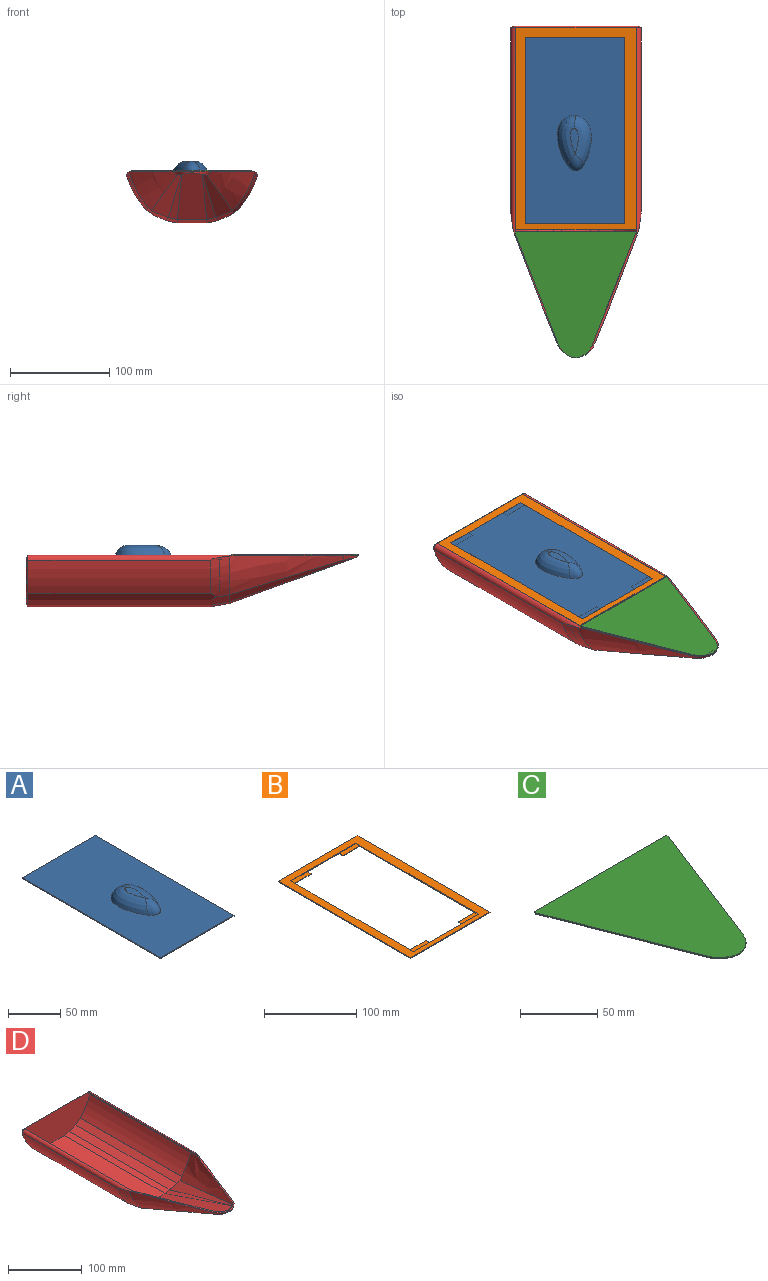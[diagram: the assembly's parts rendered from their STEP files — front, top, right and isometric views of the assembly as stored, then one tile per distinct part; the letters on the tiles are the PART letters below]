
ASSEMBLY  parts=4 mates=3
PART A: 10 faces, bbox 99.6x187.7x11.2 mm
  f0: plane 99.57x1mm, normal (0,-1,0), area 99.6mm2, adj f1,f3,f4,f5
  f1: plane 187.68x1mm, normal (1,0,0), area 187.7mm2, adj f0,f2,f4,f5
  f2: plane 99.57x1mm, normal (0,1,0), area 99.6mm2, adj f1,f3,f4,f5
  f3: plane 187.68x1mm, normal (-1,0,0), area 187.7mm2, adj f0,f2,f4,f5
  f4: plane 187.7x99.59mm, normal (0,0,1), area 17219.9mm2, adj f0,f1,f2,f3,f7,f8,f9
  f5: plane 187.68x99.57mm, normal (0,0,-1), area 18687mm2, adj f0,f1,f2,f3
  f6: plane 25.18x8.13mm, normal (0,0,1), area 142.3mm2, adj f8,f9
  f7: bspline ~17.72x17.36mm, area 167.8mm2, adj f4,f8,f9
  f8: bspline ~51.33x20.86mm, area 843.1mm2, adj f4,f6,f7,f9
  f9: bspline ~53.14x52.57mm, area 796.2mm2, adj f4,f6,f7,f8
PART B: 22 faces, bbox 121.4x203.3x1 mm
  f0: plane 99.65x1mm, normal (0,-1,0), area 74.2mm2, adj f1,f3,f4,f9,f13,f15,f19,f21
  f1: plane 187.75x1mm, normal (-1,0,0), area 182mm2, adj f0,f2,f3,f4,f16,f17,f19,f20
  f2: plane 99.65x1mm, normal (0,1,0), area 74.2mm2, adj f1,f3,f4,f9,f10,f12,f16,f18
  f3: plane 203.28x121.38mm, normal (0,0,1), area 5964.9mm2, adj f0,f1,f2,f5,f6,f7,f8,f9
  f4: plane 203.28x121.38mm, normal (0,0,-1), area 6545.5mm2, adj f0,f1,f2,f5,f6,f7,f8,f9
  f5: plane 121.38x1mm, normal (0,1,0), area 121.4mm2, adj f3,f4,f6,f8
  f6: plane 203.28x1mm, normal (-1,0,0), area 203.3mm2, adj f3,f4,f5,f7
  f7: plane 121.38x1mm, normal (0,-1,0), area 121.4mm2, adj f3,f4,f6,f8
  f8: plane 203.28x1mm, normal (1,0,0), area 203.3mm2, adj f3,f4,f5,f7
  f9: plane 187.75x1mm, normal (1,0,0), area 182mm2, adj f0,f2,f3,f4,f10,f11,f13,f14
  f10: plane 25.4x5.49mm, normal (0,0,1), area 139.3mm2, adj f2,f9,f11,f12
  f11: plane 25.4x0.5mm, normal (0,1,0), area 12.7mm2, adj f4,f9,f10,f12
  f12: plane 5.49x0.5mm, normal (1,0,0), area 2.7mm2, adj f2,f4,f10,f11
  f13: plane 25.4x5.93mm, normal (0,0,1), area 150.7mm2, adj f0,f9,f14,f15
  f14: plane 25.4x0.5mm, normal (0,-1,0), area 12.7mm2, adj f4,f9,f13,f15
  f15: plane 5.93x0.5mm, normal (1,0,0), area 3mm2, adj f0,f4,f13,f14
  f16: plane 25.4x5.49mm, normal (0,0,1), area 139.5mm2, adj f1,f2,f17,f18
  f17: plane 25.4x0.5mm, normal (0,1,0), area 12.7mm2, adj f1,f4,f16,f18
  f18: plane 5.49x0.5mm, normal (-1,0,0), area 2.7mm2, adj f2,f4,f16,f17
  f19: plane 25.4x5.95mm, normal (0,0,1), area 151.1mm2, adj f0,f1,f20,f21
  f20: plane 25.4x0.5mm, normal (0,-1,0), area 12.7mm2, adj f1,f4,f19,f21
  f21: plane 5.95x0.5mm, normal (-1,0,0), area 3mm2, adj f0,f4,f19,f20
PART C: 22 faces, bbox 121.4x127.1x1 mm
  f0: plane 3.17x2.58mm, normal (0.78,-0.63,0), area 4.1mm2, adj f1,f19,f20,f21
  f1: plane 3.93x1.98mm, normal (0.89,-0.45,0), area 4.4mm2, adj f0,f2,f20,f21
  f2: plane 112.42x43.9mm, normal (0.93,-0.36,0), area 120.7mm2, adj f1,f3,f20,f21
  f3: plane 1.79x1mm, normal (1,0,0), area 1.8mm2, adj f2,f4,f20,f21
  f4: plane 121.38x1mm, normal (0,1,0), area 121.4mm2, adj f3,f5,f20,f21
  f5: plane 1.79x1mm, normal (-1,0,0), area 1.8mm2, adj f4,f6,f20,f21
  f6: plane 112.43x43.91mm, normal (-0.93,-0.36,0), area 120.7mm2, adj f5,f7,f20,f21
  f7: plane 3.72x1.85mm, normal (-0.9,-0.45,0), area 4.2mm2, adj f6,f8,f20,f21
  f8: plane 3.05x2.39mm, normal (-0.79,-0.62,0), area 3.9mm2, adj f7,f9,f20,f21
  f9: plane 2.28x2.03mm, normal (-0.67,-0.75,0), area 3.1mm2, adj f8,f10,f20,f21
  f10: plane 3.1x1.93mm, normal (-0.53,-0.85,0), area 3.7mm2, adj f9,f11,f20,f21
  f11: plane 3.24x1.33mm, normal (-0.38,-0.93,0), area 3.5mm2, adj f10,f12,f20,f21
  f12: plane 1x0mm, normal (-0.31,-0.95,0), area 0mm2, adj f11,f13,f20,f21
  f13: plane 4.52x1mm, normal (-0.19,-0.98,0), area 4.6mm2, adj f12,f14,f20,f21
  f14: plane 3.18x1mm, normal (0.25,-0.97,0), area 3.3mm2, adj f13,f15,f20,f21
  f15: plane 1x0mm, normal (0.31,-0.95,0), area 0mm2, adj f14,f16,f20,f21
  f16: plane 3.38x1.37mm, normal (0.38,-0.93,0), area 3.6mm2, adj f15,f17,f20,f21
  f17: plane 2.88x1.76mm, normal (0.52,-0.85,0), area 3.4mm2, adj f16,f18,f20,f21
  f18: plane 2.19x1.88mm, normal (0.65,-0.76,0), area 2.9mm2, adj f17,f19,f20,f21
  f19: plane 1x0mm, normal (0.7,-0.71,0), area 0mm2, adj f0,f18,f20,f21
  f20: plane 127.13x121.38mm, normal (0,0,1), area 9226.7mm2, adj f0,f1,f2,f3,f4,f5,f6,f7
  f21: plane 127.13x121.38mm, normal (0,0,-1), area 9226.7mm2, adj f0,f1,f2,f3,f4,f5,f6,f7
PART D: 82 faces, bbox 138.5x340.2x68.2 mm
  f0: plane 127.52x49.15mm, normal (0,-1,0), area 5014.4mm2, adj f30,f31,f32,f33,f34,f35,f51,f52
  f1: plane 131.46x47.85mm, normal (0.18,0.34,0.92), area 690.9mm2, adj f6,f41,f44,f52,f55
  f2: plane 131.66x47.88mm, normal (-0.18,0.34,0.92), area 693mm2, adj f5,f6,f45,f54,f56
  f3: plane 4.3x3.32mm, normal (0.69,0.68,-0.25), area 0.6mm2, adj f4,f5,f46,f53,f62
  f4: plane 12.11x4.92mm, normal (0.14,0.93,-0.34), area 0.5mm2, adj f3,f5,f53,f54
  f5: plane 131.37x46.12mm, normal (-0.35,0.34,0.87), area 1502.5mm2, adj f2,f3,f4,f46,f47,f54
  f6: plane 137.09x49.94mm, normal (0,0.34,0.94), area 3595.6mm2, adj f1,f2,f48,f49,f50,f55,f56
  f7: plane 127.52x48.13mm, normal (0,1,0), area 4861.3mm2, adj f70,f71,f72,f73,f74,f75,f76,f77
  f8: plane 132.55x126.4mm, normal (0,0,1), area 603.8mm2, adj f9,f10,f20,f21,f27,f28,f29,f36
  f9: cylinder r=5.08mm len=210.92mm, axis (0,1,0), area 1581.9mm2, adj f8,f12,f20,f30,f69,f75
  f10: cylinder r=5.08mm len=210.92mm, axis (0,-1,0), area 1581.9mm2, adj f8,f11,f21,f31,f63,f79
  f11: cylinder r=90.14mm len=183.49mm, axis (0,-1,0), area 7050.9mm2, adj f10,f16,f63,f81
  f12: cylinder r=90.14mm len=183.49mm, axis (0,-1,0), area 7050.9mm2, adj f9,f19,f69,f73
  f13: plane 183.49x30.16mm, normal (0,0,-1), area 5534.2mm2, adj f17,f18,f66,f74
  f14: plane 183.49x12.53mm, normal (0.38,0,-0.93), area 2480.9mm2, adj f16,f17,f64,f78
  f15: plane 183.49x12.53mm, normal (-0.38,0,-0.93), area 2480.9mm2, adj f18,f19,f68,f70
  f16: plane 190.94x10.1mm, normal (0.58,0,-0.82), area 2211.8mm2, adj f11,f14,f63,f64,f80
  f17: plane 183.49x9.79mm, normal (0.19,0,-0.98), area 1829.7mm2, adj f13,f14,f65,f76
  f18: plane 183.49x9.79mm, normal (-0.19,0,-0.98), area 1829.7mm2, adj f13,f15,f67,f72
  f19: plane 190.94x10.1mm, normal (-0.58,0,-0.82), area 2211.8mm2, adj f12,f15,f68,f69,f71
  f20: cone r=39.34mm half-angle=20deg, axis (0,1,0), area 2911.3mm2, adj f8,f9,f22,f28,f69
  f21: cone r=39.34mm half-angle=20deg, axis (0,1,0), area 2911.3mm2, adj f8,f10,f23,f27,f63
  f22: plane 125.53x45.78mm, normal (-0.35,-0.34,-0.87), area 1417.5mm2, adj f20,f24,f28,f68
  f23: plane 125.53x45.78mm, normal (0.35,-0.34,-0.87), area 1417.5mm2, adj f21,f25,f27,f64
  f24: plane 123.63x45.01mm, normal (-0.18,-0.34,-0.92), area 650.4mm2, adj f22,f26,f28,f67
  f25: plane 123.63x45.01mm, normal (0.18,-0.34,-0.92), area 650.4mm2, adj f23,f26,f27,f65
  f26: plane 129.12x47.14mm, normal (0,-0.34,-0.94), area 3381.9mm2, adj f24,f25,f27,f28,f29,f66
  f27: bspline ~30.3x29.89mm, area 83.6mm2, adj f8,f21,f23,f25,f26,f29
  f28: bspline ~30.3x29.89mm, area 83.6mm2, adj f8,f20,f22,f24,f26,f29
  f29: bspline ~4.91x2.67mm, area 3.8mm2, adj f8,f26,f27,f28
  f30: plane 205.11x2.03mm, normal (1,0,0), area 408.7mm2, adj f0,f9,f32,f36
  f31: plane 205.1x2.03mm, normal (-1,0,0), area 408.7mm2, adj f0,f10,f33,f37
  f32: cylinder r=3.08mm len=203.6mm, axis (0,1,0), area 907mm2, adj f0,f30,f35,f36
  f33: cylinder r=3.08mm len=203.6mm, axis (0,-1,0), area 907mm2, adj f0,f31,f34,f37
  f34: cylinder r=88.14mm len=193.3mm, axis (0,-1,0), area 7153.1mm2, adj f0,f33,f37,f59
  f35: cylinder r=88.14mm len=193.3mm, axis (0,-1,0), area 7153.1mm2, adj f0,f32,f36,f57
  f36: cone r=37.46mm half-angle=20deg, axis (0,1,0), area 3397.3mm2, adj f8,f30,f32,f35,f39,f42,f58
  f37: cone r=37.46mm half-angle=20deg, axis (0,1,0), area 3397.3mm2, adj f8,f31,f33,f34,f38,f46,f61
  f38: offset ~34.38x33.97mm, area 41.1mm2, adj f8,f37,f40,f45,f47,f48
  f39: offset ~34.38x33.97mm, area 41.1mm2, adj f8,f36,f40,f41,f43,f49
  f40: bspline ~2.49x1.35mm, area 0.3mm2, adj f8,f38,f39,f50
  f41: extruded ~1.01x0.7mm, area 0.5mm2, adj f1,f39,f43,f49
  f42: extruded ~121.25x37.81mm, area 128.8mm2, adj f36,f43,f44,f58
  f43: extruded ~7.45x3.96mm, area 8.3mm2, adj f39,f41,f42,f44
  f44: plane 131.07x46.02mm, normal (0.35,0.34,0.87), area 1496mm2, adj f1,f42,f43,f51,f52,f58
  f45: extruded ~1.01x0.7mm, area 0.5mm2, adj f2,f38,f47,f48
  f46: extruded ~121.25x37.81mm, area 128.7mm2, adj f3,f5,f37,f47,f60,f62
  f47: extruded ~7.45x3.96mm, area 8.3mm2, adj f5,f38,f45,f46
  f48: extruded ~9.64x5.75mm, area 11.4mm2, adj f6,f38,f45,f50
  f49: extruded ~9.64x5.75mm, area 11.4mm2, adj f6,f39,f41,f50
  f50: extruded ~1.23x0.96mm, area 1.2mm2, adj f6,f40,f48,f49
  f51: plane 196.57x9.28mm, normal (0.58,0,0.82), area 2214.8mm2, adj f0,f44,f52,f57,f58
  f52: plane 193.26x12.13mm, normal (0.38,0,0.93), area 2531.1mm2, adj f0,f1,f44,f51,f55
  f53: plane 193.14x12.13mm, normal (-0.38,0,0.93), area 2527.3mm2, adj f0,f3,f4,f54,f62
  f54: plane 192.97x9.41mm, normal (-0.19,0,0.98), area 1849.5mm2, adj f0,f2,f4,f5,f53,f56
  f55: plane 193.17x9.41mm, normal (0.19,0,0.98), area 1851.4mm2, adj f0,f1,f6,f52,f56
  f56: plane 193.07x29.77mm, normal (0,0,1), area 5748.4mm2, adj f0,f2,f6,f54,f55
  f57: plane 193.3x0.98mm, normal (-0.98,0,0.19), area 193.3mm2, adj f0,f35,f51,f58
  f58: extruded ~5.17x4.5mm, area 6.4mm2, adj f36,f42,f44,f51,f57
  f59: plane 193.3x0.98mm, normal (0.98,0,-0.19), area 193.3mm2, adj f0,f34,f61,f62
  f60: plane 0.98x0.22mm, normal (-0.66,-0.74,0.13), area 0.1mm2, adj f46,f61,f62
  f61: extruded ~5.17x4.5mm, area 5.3mm2, adj f37,f59,f60,f62
  f62: plane 196.74x9.43mm, normal (-0.58,0,0.82), area 2214.2mm2, adj f0,f3,f46,f53,f59,f60,f61
  f63: cone r=90.14mm half-angle=10deg, axis (0,1,0), area 887.4mm2, adj f10,f11,f16,f21,f64
  f64: plane 19.71x17.96mm, normal (0.37,-0.17,-0.91), area 351.4mm2, adj f14,f16,f23,f63,f65
  f65: plane 19.71x10.12mm, normal (0.19,-0.17,-0.97), area 192.8mm2, adj f17,f25,f64,f66
  f66: plane 30.16x19.71mm, normal (0,-0.17,-0.98), area 596.8mm2, adj f13,f26,f65,f67
  f67: plane 19.71x10.12mm, normal (-0.19,-0.17,-0.97), area 192.8mm2, adj f18,f24,f66,f68
  f68: plane 19.71x17.96mm, normal (-0.37,-0.17,-0.91), area 351.4mm2, adj f15,f19,f22,f67,f69
  f69: cone r=90.14mm half-angle=10deg, axis (0,1,0), area 887.4mm2, adj f9,f12,f19,f20,f68
  f70: plane 13.1x6.85mm, normal (-0.27,0.71,-0.66), area 37.6mm2, adj f7,f15,f71,f72
  f71: plane 10.62x8.32mm, normal (-0.41,0.71,-0.58), area 32.8mm2, adj f7,f19,f70,f73
  f72: plane 9.98x3.84mm, normal (-0.14,0.71,-0.69), area 27.7mm2, adj f7,f18,f70,f74
  f73: cone r=88.14mm half-angle=45deg, axis (0,-1,0), area 106.7mm2, adj f7,f12,f71,f75
  f74: plane 30.16x2mm, normal (0,0.71,-0.71), area 84.8mm2, adj f7,f13,f72,f76
  f75: cone r=3.08mm half-angle=45deg, axis (0,-1,0), area 17.7mm2, adj f7,f9,f73,f77
  f76: plane 9.98x3.84mm, normal (0.14,0.71,-0.69), area 27.7mm2, adj f7,f17,f74,f78
  f77: plane 121.38x2mm, normal (0,0.71,0.71), area 343.3mm2, adj f0,f7,f75,f79
  f78: plane 13.1x6.85mm, normal (0.27,0.71,-0.66), area 37.6mm2, adj f7,f14,f76,f80
  f79: cone r=3.08mm half-angle=45deg, axis (0,-1,0), area 17.7mm2, adj f7,f10,f77,f81
  f80: plane 10.62x8.32mm, normal (0.41,0.71,-0.58), area 32.8mm2, adj f7,f16,f78,f81
  f81: cone r=88.14mm half-angle=45deg, axis (0,-1,0), area 106.7mm2, adj f7,f11,f79,f80
PLACE A t=(95.28,-107.05,-131.64)mm
PLACE B t=(95.2,-107.06,-130.56)mm
PLACE C rot(axis=(0,0,1),0deg) t=(94.6,-109.16,-129.56)mm
PLACE D rot(axis=(0,0,1),0deg) t=(95.2,-107.06,-129.56)mm
MATE fastened D.f0 <-> B.f5  axis (0,-1,0) through (15.92,125.36,-60.98)mm
MATE slider A.f5 <-> B.f19  axis (0,0,-1) through (125.77,116.15,-62.06)mm
MATE revolute D.f8 <-> C.f21  axis (0,0,1) through (76.61,-207.16,-60.98)mm
